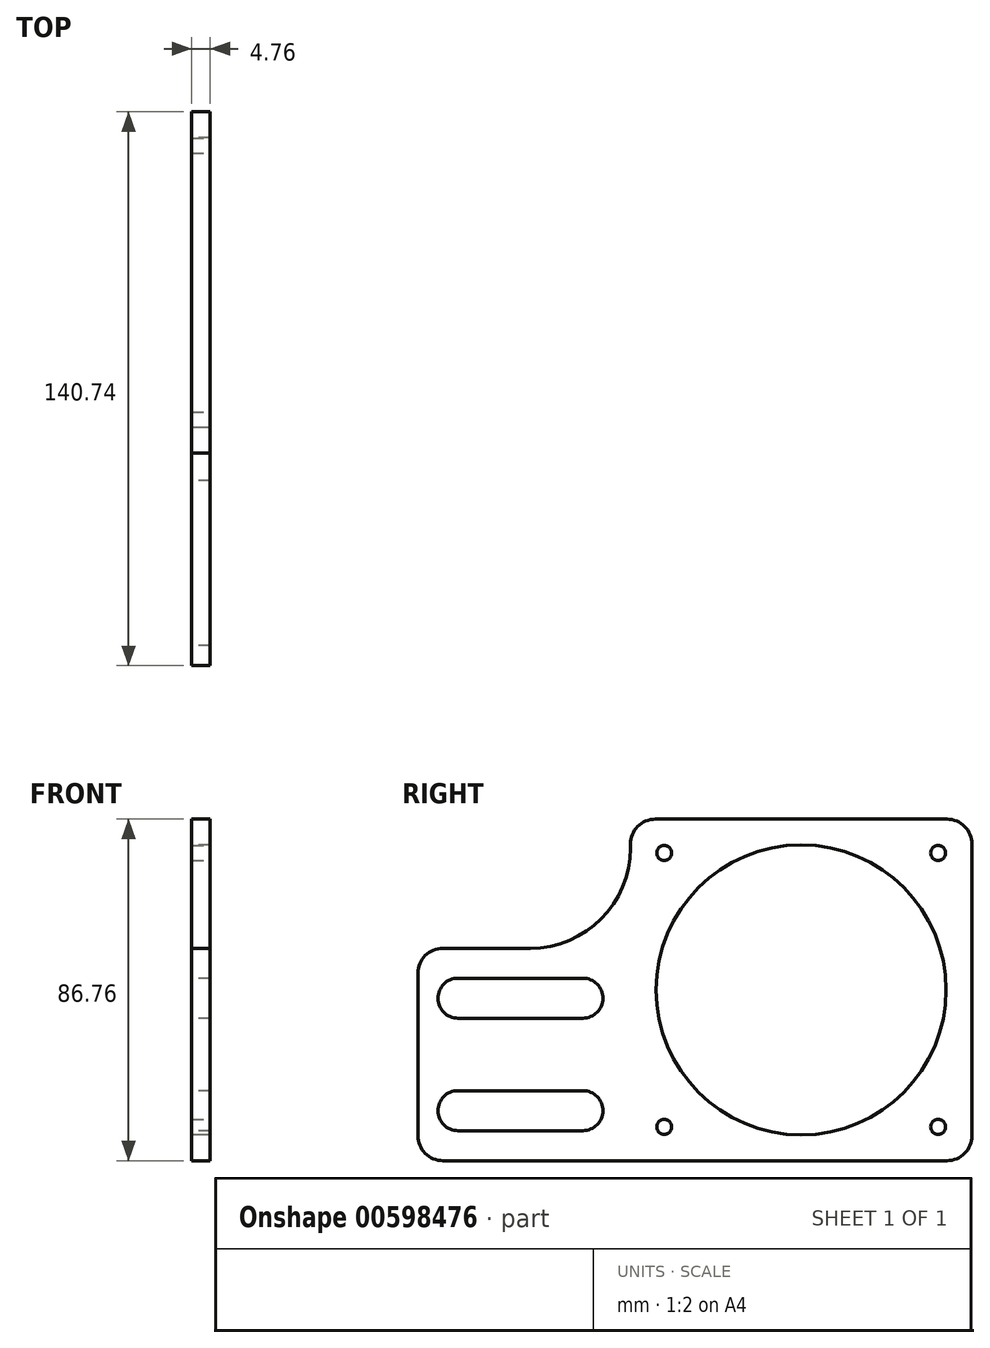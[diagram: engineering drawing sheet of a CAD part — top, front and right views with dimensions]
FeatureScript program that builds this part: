
annotation { "Feature Type Name" : "Feature", "Feature Type Description" : "" }
export const myFeature = defineFeature(function(context is Context, id is Id, definition is map)
    precondition{}
    {
        {
            var Q0;
            Q0=qCreatedBy(makeId("Right.planeOp"),FACE);
            var sketch = newSketch(context, id + "F0", { "sketchPlane" : qUnion([Q0])});
            skLineSegment(sketch, "E0.bottom", {"start": v(37.03, 43.38) * mm, "end": v(-37.03, 43.38) * mm});
            skLineSegment(sketch, "E0.top", {"start": v(37.03, -43.38) * mm, "end": v(-43.38, -43.38) * mm});
            skLineSegment(sketch, "E0.left", {"start": v(43.38, 37.03) * mm, "end": v(43.38, -37.03) * mm});
            skLineSegment(sketch, "E0.right", {"start": v(-43.38, 37.03) * mm, "end": v(-43.38, 36) * mm});
            skPoint(sketch, "E0.middle", {"position": v(0, 0) * mm});
            skCircle(sketch, "E1", {"center": v(0, 0) * mm, "radius": 36.83 * mm});
            skCircle(sketch, "E2", {"center": v(0, 0) * mm, "radius": 49.21 * mm, "construction": true});
            skLineSegment(sketch, "E3", {"start": v(-43.38, 43.38) * mm, "end": v(43.38, -43.38) * mm, "construction": true});
            skLineSegment(sketch, "E4", {"start": v(43.38, 43.38) * mm, "end": v(-43.38, -43.38) * mm, "construction": true});
            skPoint(sketch, "E5", {"position": v(-34.8, 34.8) * mm});
            skPoint(sketch, "E6", {"position": v(34.8, 34.8) * mm});
            skPoint(sketch, "E7", {"position": v(-34.8, -34.8) * mm});
            skPoint(sketch, "E8", {"position": v(34.8, -34.8) * mm});
            skLineSegment(sketch, "E9", {"start": v(-43.38, -43.38) * mm, "end": v(-91, -43.38) * mm});
            skLineSegment(sketch, "E10", {"start": v(-97.36, -37.03) * mm, "end": v(-97.36, 4.24) * mm});
            skLineSegment(sketch, "E11", {"start": v(-91, 10.6) * mm, "end": v(-68.78, 10.6) * mm});
            skPoint(sketch, "E12.visualSharp", {"position": v(-97.36, 10.6) * mm});
            skArc(sketch, "E12.filletArc", {"start": v(-91, 10.6) * mm, "mid": v(-95.5, 8.73) * mm, "end": v(-97.36, 4.24) * mm});
            skPoint(sketch, "E13.visualSharp", {"position": v(-97.36, -43.38) * mm});
            skArc(sketch, "E13.filletArc", {"start": v(-97.36, -37.03) * mm, "mid": v(-95.5, -41.52) * mm, "end": v(-91, -43.38) * mm});
            skPoint(sketch, "E14.visualSharp", {"position": v(43.38, -43.38) * mm});
            skArc(sketch, "E14.filletArc", {"start": v(37.03, -43.38) * mm, "mid": v(41.52, -41.52) * mm, "end": v(43.38, -37.03) * mm});
            skPoint(sketch, "E15.visualSharp", {"position": v(-43.38, 43.38) * mm});
            skArc(sketch, "E15.filletArc", {"start": v(-37.03, 43.38) * mm, "mid": v(-41.52, 41.52) * mm, "end": v(-43.38, 37.03) * mm});
            skPoint(sketch, "E16.visualSharp", {"position": v(43.38, 43.38) * mm});
            skArc(sketch, "E16.filletArc", {"start": v(43.38, 37.03) * mm, "mid": v(41.52, 41.52) * mm, "end": v(37.03, 43.38) * mm});
            skPoint(sketch, "E17.visualSharp", {"position": v(-43.38, 10.6) * mm});
            skArc(sketch, "E17.filletArc", {"start": v(-68.78, 10.6) * mm, "mid": v(-50.82, 18.03) * mm, "end": v(-43.38, 36) * mm});
            skLineSegment(sketch, "E18", {"start": v(-87.2, -2.1) * mm, "end": v(-55.45, -2.1) * mm});
            skLineSegment(sketch, "E19", {"start": v(-87.2, -30.68) * mm, "end": v(-55.45, -30.68) * mm});
            skArc(sketch, "E20.0.startCap", {"start": v(-87.2, -7.19) * mm, "mid": v(-92.28, -2.1) * mm, "end": v(-87.2, 2.97) * mm});
            skArc(sketch, "E20.0.endCap", {"start": v(-55.45, 2.97) * mm, "mid": v(-50.37, -2.1) * mm, "end": v(-55.45, -7.19) * mm});
            skLineSegment(sketch, "E20.0.left", {"start": v(-87.2, 2.97) * mm, "end": v(-55.45, 2.97) * mm});
            skLineSegment(sketch, "E20.0.right", {"start": v(-87.2, -7.19) * mm, "end": v(-55.45, -7.19) * mm});
            skArc(sketch, "E21.0.startCap", {"start": v(-87.2, -35.76) * mm, "mid": v(-92.28, -30.68) * mm, "end": v(-87.2, -25.6) * mm});
            skArc(sketch, "E21.0.endCap", {"start": v(-55.45, -25.6) * mm, "mid": v(-50.37, -30.68) * mm, "end": v(-55.45, -35.76) * mm});
            skLineSegment(sketch, "E21.0.left", {"start": v(-87.2, -25.6) * mm, "end": v(-55.45, -25.6) * mm});
            skLineSegment(sketch, "E21.0.right", {"start": v(-87.2, -35.76) * mm, "end": v(-55.45, -35.76) * mm});
            skSolve(sketch);
        }
        {
            var Q0;
            Q0=makeQuery(id+"F0.imprint","IMPRINT",FACE,{"disambiguationData":[TD([[makeQuery(id+"F0.imprint","IMPRINT",EDGE,{"derivedFrom":sQuery(id+"F0.wireOp",EDGE,"E0.bottom")}),1.0]])]});
            extrude(context, id + "F1", {"entities" : qUnion([Q0]), "depth" : 4.76 * mm, "offsetDistance" : 25.4 * mm});
        }
        {
            var Q0;
            Q0=sQuery(id+"F0.wireOp",VERTEX,"E6");
            var Q1;
            Q1=sQuery(id+"F0.wireOp",VERTEX,"E8");
            var Q2;
            Q2=sQuery(id+"F0.wireOp",VERTEX,"E7");
            var Q3;
            Q3=sQuery(id+"F0.wireOp",VERTEX,"E5");
            var Q4;
            Q4=makeQuery(id+"F1.opExtrude","SWEPT_BODY",BODY,{"disambiguationData":[OSD([sQuery(id+"F0.wireOp",EDGE,"E0.bottom"),sQuery(id+"F0.wireOp",EDGE,"E0.top"),sQuery(id+"F0.wireOp",EDGE,"E0.left"),sQuery(id+"F0.wireOp",EDGE,"E0.right"),sQuery(id+"F0.wireOp",EDGE,"E1")])]});
            hole(context, id + "F2", {"style" : HoleStyle.SIMPLE, "endStyle" : HoleEndStyle.THROUGH, "oppositeDirection" : true, "standardTappedOrClearance" : lookupTablePath({ "standard" : "ANSI", "engagement" : "75%", "pitch" : "24 tpi", "size" : "#10", "type" : "Tapped" }), "standardBlindInLast" : lookupTablePath({ "standard" : "ANSI", "engagement" : "75%", "pitch" : "24 tpi", "size" : "#10", "type" : "Tapped" }), "holeDiameter" : 3.8 * mm, "majorDiameter" : 4.83 * mm, "showTappedDepth" : true, "isTappedThrough" : true, "tappedDepth" : 12.7 * mm, "tapClearance" : 3, "locations" : qUnion([Q0, Q1, Q2, Q3]), "scope" : qUnion([Q4]), "startStyle" : HoleStartStyle.PART});
        }
    });
